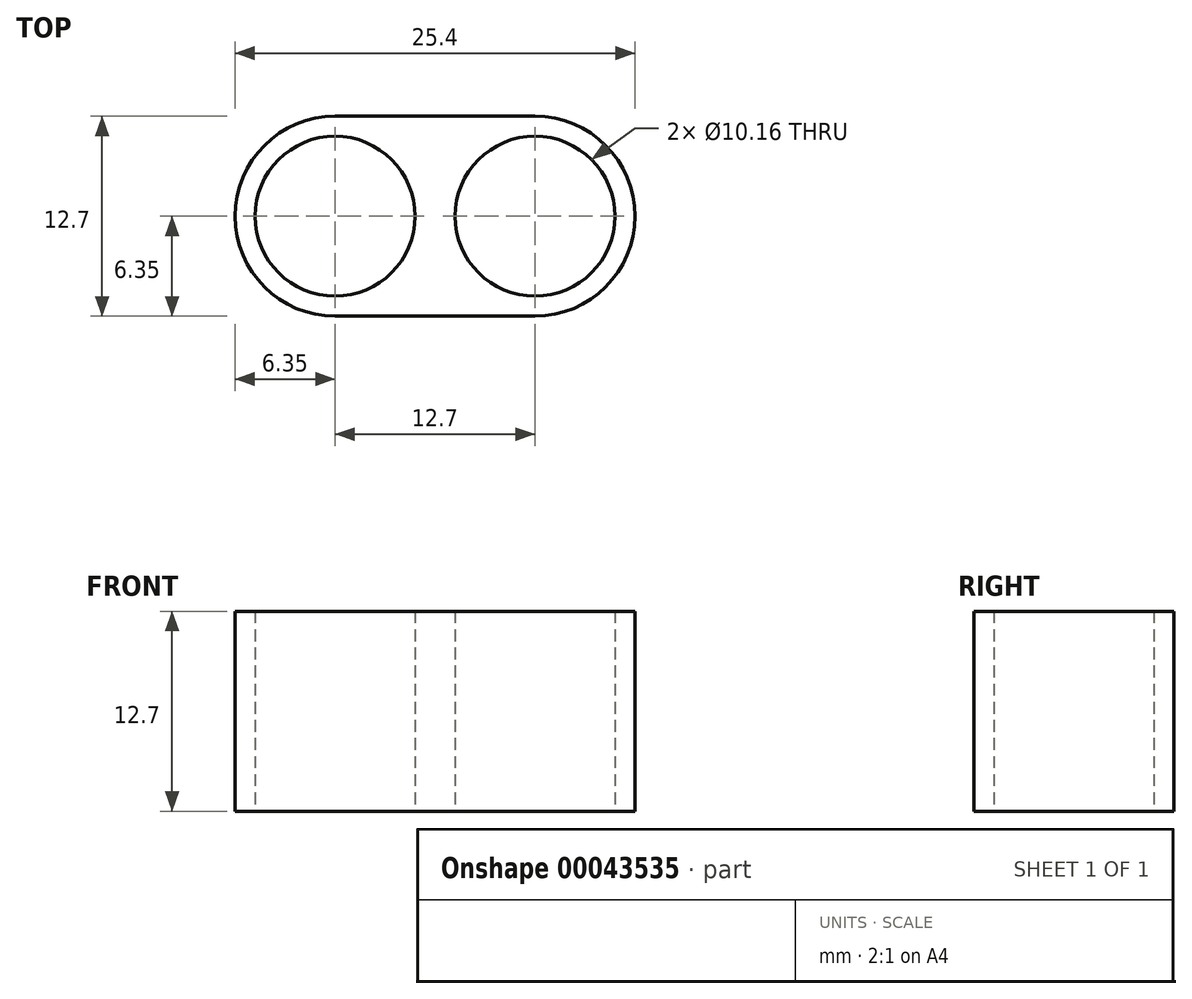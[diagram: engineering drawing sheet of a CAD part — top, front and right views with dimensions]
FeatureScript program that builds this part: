
annotation { "Feature Type Name" : "Feature", "Feature Type Description" : "" }
export const myFeature = defineFeature(function(context is Context, id is Id, definition is map)
    precondition{}
    {
        {
            var Q0;
            Q0=qCreatedBy(makeId("Top.planeOp"),FACE);
            var sketch = newSketch(context, id + "F0", { "sketchPlane" : qUnion([Q0])});
            skPoint(sketch, "E0", {"position": v(25.4, 0) * mm});
            skPoint(sketch, "E1", {"position": v(25.4, 12.7) * mm});
            skLineSegment(sketch, "E2.bottom", {"start": v(6.35, 0) * mm, "end": v(19.05, 0) * mm});
            skLineSegment(sketch, "E2.top", {"start": v(0, 12.7) * mm, "end": v(25.4, 12.7) * mm});
            skLineSegment(sketch, "E2.left", {"start": v(0, 6.35) * mm, "end": v(0, 6.35) * mm});
            skLineSegment(sketch, "E2.right", {"start": v(25.4, 6.35) * mm, "end": v(25.4, 6.35) * mm});
            skPoint(sketch, "E3", {"position": v(12.7, 12.7) * mm});
            skPoint(sketch, "E4", {"position": v(12.7, 6.35) * mm});
            skPoint(sketch, "E4.positionSnap0", {"position": v(0, 6.35) * mm});
            skLineSegment(sketch, "E5", {"start": v(12.7, 12.7) * mm, "end": v(19.05, 12.7) * mm});
            skLineSegment(sketch, "E6", {"start": v(6.35, 12.7) * mm, "end": v(12.7, 12.7) * mm});
            skPoint(sketch, "E7", {"position": v(6.35, 6.35) * mm});
            skPoint(sketch, "E7.positionSnap0", {"position": v(6.35, 12.7) * mm});
            skPoint(sketch, "E8", {"position": v(19.05, 6.35) * mm});
            skPoint(sketch, "E8.positionSnap0", {"position": v(19.05, 12.7) * mm});
            skPoint(sketch, "E9", {"position": v(1.27, 6.35) * mm});
            skPoint(sketch, "E10", {"position": v(24.13, 6.35) * mm});
            skCircle(sketch, "E11", {"center": v(6.35, 6.35) * mm, "radius": 5.08 * mm});
            skCircle(sketch, "E12", {"center": v(19.05, 6.35) * mm, "radius": 5.08 * mm});
            skPoint(sketch, "E13.visualSharp", {"position": v(0, 12.7) * mm});
            skArc(sketch, "E13.filletArc", {"start": v(6.35, 12.7) * mm, "mid": v(1.86, 10.84) * mm, "end": v(0, 6.35) * mm});
            skArc(sketch, "E14.filletArc", {"start": v(19.05, 0) * mm, "mid": v(23.54, 1.86) * mm, "end": v(25.4, 6.35) * mm});
            skArc(sketch, "E15.filletArc", {"start": v(25.4, 6.35) * mm, "mid": v(23.54, 10.84) * mm, "end": v(19.05, 12.7) * mm});
            skPoint(sketch, "E16.visualSharp", {"position": v(0, 0) * mm});
            skArc(sketch, "E16.filletArc", {"start": v(0, 6.35) * mm, "mid": v(1.86, 1.86) * mm, "end": v(6.35, 0) * mm});
            skSolve(sketch);
        }
        {
            var Q0;
            Q0 = qSketchRegion(id + "F0", true);
            extrude(context, id + "F1", {"entities" : qUnion([Q0]), "depth" : 12.7 * mm});
        }
    });
